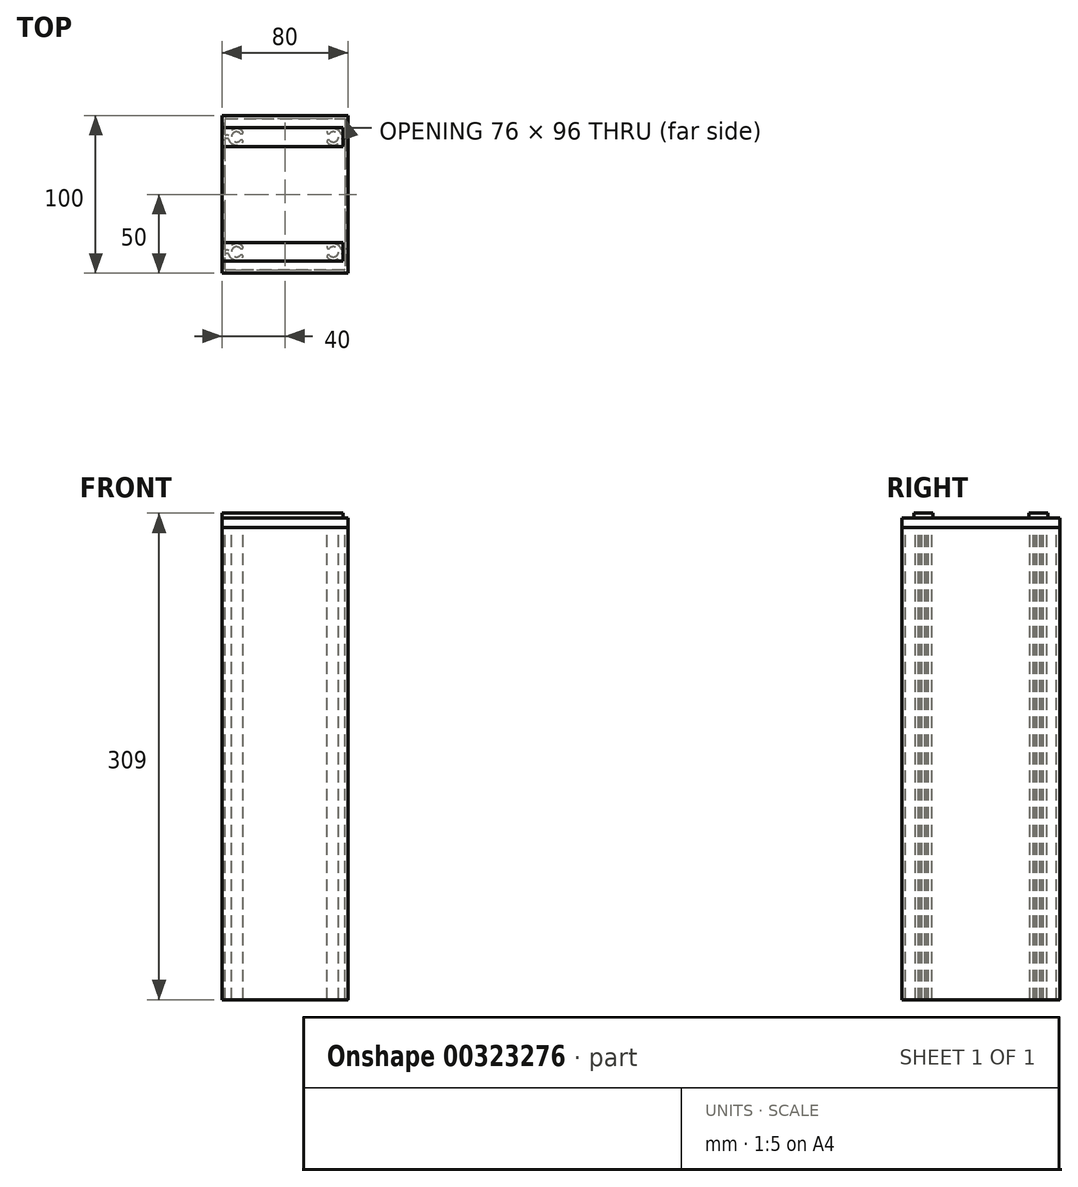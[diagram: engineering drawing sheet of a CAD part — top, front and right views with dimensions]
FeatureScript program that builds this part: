
annotation { "Feature Type Name" : "Feature", "Feature Type Description" : "" }
export const myFeature = defineFeature(function(context is Context, id is Id, definition is map)
    precondition{}
    {
        {
            var Q0;
            Q0=qCreatedBy(makeId("Top.planeOp"),FACE);
            var sketch = newSketch(context, id + "F0", { "sketchPlane" : qUnion([Q0])});
            skLineSegment(sketch, "E0", {"start": v(40, 49.5) * mm, "end": v(40, -49.5) * mm});
            skLineSegment(sketch, "E1", {"start": v(39.5, -50) * mm, "end": v(-39.5, -50) * mm});
            skLineSegment(sketch, "E2", {"start": v(-40, -49.5) * mm, "end": v(-40, 49.5) * mm});
            skLineSegment(sketch, "E3", {"start": v(-39.5, 50) * mm, "end": v(39.5, 50) * mm});
            skLineSegment(sketch, "E4", {"start": v(38, 47.5) * mm, "end": v(38, 38) * mm});
            skLineSegment(sketch, "E5", {"start": v(-37.5, 48) * mm, "end": v(37.5, 48) * mm});
            skLineSegment(sketch, "E6", {"start": v(37.5, -48) * mm, "end": v(-37.5, -48) * mm});
            skLineSegment(sketch, "E7", {"start": v(-38, -47.5) * mm, "end": v(-38, -38) * mm});
            skArc(sketch, "E8", {"start": v(28.4, -38.74) * mm, "mid": v(34, -36.5) * mm, "end": v(28.4, -34.26) * mm});
            skArc(sketch, "E9", {"start": v(28.4, -38.74) * mm, "mid": v(27.82, -38.44) * mm, "end": v(27.17, -38.57) * mm});
            skArc(sketch, "E10", {"start": v(27.17, -34.43) * mm, "mid": v(27.82, -34.56) * mm, "end": v(28.4, -34.26) * mm});
            skArc(sketch, "E11", {"start": v(26.95, -40.12) * mm, "mid": v(32.04, -41.59) * mm, "end": v(35.82, -37.87) * mm});
            skArc(sketch, "E12", {"start": v(27.17, -38.57) * mm, "mid": v(26.68, -39.29) * mm, "end": v(26.95, -40.12) * mm});
            skArc(sketch, "E13", {"start": v(26.95, -32.88) * mm, "mid": v(26.68, -33.71) * mm, "end": v(27.17, -34.43) * mm});
            skLineSegment(sketch, "E14", {"start": v(27.17, -34.43) * mm, "end": v(30.75, -36.5) * mm, "construction": true});
            skLineSegment(sketch, "E15", {"start": v(30.75, -36.5) * mm, "end": v(27.17, -38.57) * mm, "construction": true});
            skArc(sketch, "E16", {"start": v(28.4, 34.26) * mm, "mid": v(34, 36.5) * mm, "end": v(28.4, 38.74) * mm});
            skArc(sketch, "E17", {"start": v(28.4, 34.26) * mm, "mid": v(27.82, 34.56) * mm, "end": v(27.17, 34.43) * mm});
            skArc(sketch, "E18", {"start": v(27.17, 38.57) * mm, "mid": v(27.82, 38.44) * mm, "end": v(28.4, 38.74) * mm});
            skArc(sketch, "E19", {"start": v(26.95, 32.88) * mm, "mid": v(32.04, 31.41) * mm, "end": v(35.82, 35.13) * mm});
            skArc(sketch, "E20", {"start": v(27.17, 34.43) * mm, "mid": v(26.68, 33.71) * mm, "end": v(26.95, 32.88) * mm});
            skArc(sketch, "E21", {"start": v(26.95, 40.12) * mm, "mid": v(26.68, 39.29) * mm, "end": v(27.17, 38.57) * mm});
            skLineSegment(sketch, "E22", {"start": v(27.17, 38.57) * mm, "end": v(30.75, 36.5) * mm, "construction": true});
            skLineSegment(sketch, "E23", {"start": v(30.75, 36.5) * mm, "end": v(27.17, 34.43) * mm, "construction": true});
            skArc(sketch, "E24", {"start": v(-28.4, 38.74) * mm, "mid": v(-34, 36.5) * mm, "end": v(-28.4, 34.26) * mm});
            skArc(sketch, "E25", {"start": v(-27.17, 34.43) * mm, "mid": v(-27.82, 34.56) * mm, "end": v(-28.4, 34.26) * mm});
            skArc(sketch, "E26", {"start": v(-28.4, 38.74) * mm, "mid": v(-27.82, 38.44) * mm, "end": v(-27.17, 38.57) * mm});
            skArc(sketch, "E27", {"start": v(-26.95, 40.12) * mm, "mid": v(-32.04, 41.59) * mm, "end": v(-35.82, 37.87) * mm});
            skArc(sketch, "E28", {"start": v(-26.95, 32.88) * mm, "mid": v(-26.68, 33.71) * mm, "end": v(-27.17, 34.43) * mm});
            skArc(sketch, "E29", {"start": v(-27.17, 38.57) * mm, "mid": v(-26.68, 39.29) * mm, "end": v(-26.95, 40.12) * mm});
            skLineSegment(sketch, "E30", {"start": v(-27.17, 38.57) * mm, "end": v(-30.75, 36.5) * mm, "construction": true});
            skLineSegment(sketch, "E31", {"start": v(-30.75, 36.5) * mm, "end": v(-27.17, 34.43) * mm, "construction": true});
            skArc(sketch, "E32", {"start": v(-28.4, -34.26) * mm, "mid": v(-34, -36.5) * mm, "end": v(-28.4, -38.74) * mm});
            skArc(sketch, "E33", {"start": v(-27.17, -38.57) * mm, "mid": v(-27.82, -38.44) * mm, "end": v(-28.4, -38.74) * mm});
            skArc(sketch, "E34", {"start": v(-28.4, -34.26) * mm, "mid": v(-27.82, -34.56) * mm, "end": v(-27.17, -34.43) * mm});
            skArc(sketch, "E35", {"start": v(-26.95, -32.88) * mm, "mid": v(-32.04, -31.41) * mm, "end": v(-35.82, -35.13) * mm});
            skArc(sketch, "E36", {"start": v(-26.95, -40.12) * mm, "mid": v(-26.68, -39.29) * mm, "end": v(-27.17, -38.57) * mm});
            skArc(sketch, "E37", {"start": v(-27.17, -34.43) * mm, "mid": v(-26.68, -33.71) * mm, "end": v(-26.95, -32.88) * mm});
            skLineSegment(sketch, "E38", {"start": v(-27.17, -34.43) * mm, "end": v(-30.75, -36.5) * mm, "construction": true});
            skLineSegment(sketch, "E39", {"start": v(-30.75, -36.5) * mm, "end": v(-27.17, -38.57) * mm, "construction": true});
            skLineSegment(sketch, "E40", {"start": v(37.5, 35.5) * mm, "end": v(36.3, 35.5) * mm});
            skLineSegment(sketch, "E41", {"start": v(37.5, 37.5) * mm, "end": v(36.3, 37.5) * mm});
            skLineSegment(sketch, "E42", {"start": v(37.5, -35.5) * mm, "end": v(36.3, -35.5) * mm});
            skLineSegment(sketch, "E43", {"start": v(37.5, -37.5) * mm, "end": v(36.3, -37.5) * mm});
            skLineSegment(sketch, "E44", {"start": v(38, 35) * mm, "end": v(38, -35) * mm});
            skLineSegment(sketch, "E45", {"start": v(-38, 38) * mm, "end": v(-38, 47.5) * mm});
            skLineSegment(sketch, "E46", {"start": v(-36.3, 37.5) * mm, "end": v(-37.5, 37.5) * mm});
            skLineSegment(sketch, "E47", {"start": v(-36.3, 35.5) * mm, "end": v(-37.5, 35.5) * mm});
            skArc(sketch, "E48", {"start": v(35.82, 37.87) * mm, "mid": v(32.04, 41.59) * mm, "end": v(26.95, 40.12) * mm});
            skArc(sketch, "E49", {"start": v(-35.82, 35.13) * mm, "mid": v(-32.04, 31.41) * mm, "end": v(-26.95, 32.88) * mm});
            skLineSegment(sketch, "E50", {"start": v(38, -38) * mm, "end": v(38, -47.5) * mm});
            skArc(sketch, "E51", {"start": v(35.82, -35.13) * mm, "mid": v(32.04, -31.41) * mm, "end": v(26.95, -32.88) * mm});
            skLineSegment(sketch, "E52", {"start": v(-38, -35) * mm, "end": v(-38, 35) * mm});
            skArc(sketch, "E53", {"start": v(-35.82, -37.87) * mm, "mid": v(-32.04, -41.59) * mm, "end": v(-26.95, -40.12) * mm});
            skLineSegment(sketch, "E54", {"start": v(-36.3, -35.5) * mm, "end": v(-37.5, -35.5) * mm});
            skLineSegment(sketch, "E55", {"start": v(-36.3, -37.5) * mm, "end": v(-37.5, -37.5) * mm});
            skArc(sketch, "E56", {"start": v(40, 49.5) * mm, "mid": v(39.85, 49.85) * mm, "end": v(39.5, 50) * mm});
            skArc(sketch, "E57", {"start": v(39.5, -50) * mm, "mid": v(39.85, -49.85) * mm, "end": v(40, -49.5) * mm});
            skArc(sketch, "E58", {"start": v(-39.5, 50) * mm, "mid": v(-39.85, 49.85) * mm, "end": v(-40, 49.5) * mm});
            skArc(sketch, "E59", {"start": v(-40, -49.5) * mm, "mid": v(-39.85, -49.85) * mm, "end": v(-39.5, -50) * mm});
            skLineSegment(sketch, "E60", {"start": v(0, 53) * mm, "end": v(0, -53) * mm, "construction": true});
            skLineSegment(sketch, "E61", {"start": v(34.3, 36.5) * mm, "end": v(-34.3, 36.5) * mm, "construction": true});
            skLineSegment(sketch, "E62", {"start": v(34.3, -36.5) * mm, "end": v(-34.3, -36.5) * mm, "construction": true});
            skLineSegment(sketch, "E63", {"start": v(30.75, 40.05) * mm, "end": v(30.75, 32.95) * mm, "construction": true});
            skLineSegment(sketch, "E64", {"start": v(-30.75, 40.05) * mm, "end": v(-30.75, 32.95) * mm, "construction": true});
            skLineSegment(sketch, "E65", {"start": v(-30.75, -32.95) * mm, "end": v(-30.75, -40.05) * mm, "construction": true});
            skLineSegment(sketch, "E66", {"start": v(30.75, -32.95) * mm, "end": v(30.75, -40.05) * mm, "construction": true});
            skLineSegment(sketch, "E67", {"start": v(43, 0) * mm, "end": v(-43, 0) * mm, "construction": true});
            skArc(sketch, "E68", {"start": v(38, 47.5) * mm, "mid": v(37.85, 47.85) * mm, "end": v(37.5, 48) * mm});
            skArc(sketch, "E69", {"start": v(37.5, 37.5) * mm, "mid": v(37.85, 37.65) * mm, "end": v(38, 38) * mm});
            skArc(sketch, "E70", {"start": v(35.82, 37.87) * mm, "mid": v(36, 37.6) * mm, "end": v(36.3, 37.5) * mm});
            skArc(sketch, "E71", {"start": v(36.3, 35.5) * mm, "mid": v(36, 35.4) * mm, "end": v(35.82, 35.13) * mm});
            skArc(sketch, "E72", {"start": v(38, 35) * mm, "mid": v(37.85, 35.35) * mm, "end": v(37.5, 35.5) * mm});
            skArc(sketch, "E73", {"start": v(37.5, -35.5) * mm, "mid": v(37.85, -35.35) * mm, "end": v(38, -35) * mm});
            skArc(sketch, "E74", {"start": v(35.82, -35.13) * mm, "mid": v(36, -35.4) * mm, "end": v(36.3, -35.5) * mm});
            skArc(sketch, "E75", {"start": v(38, -38) * mm, "mid": v(37.85, -37.65) * mm, "end": v(37.5, -37.5) * mm});
            skArc(sketch, "E76", {"start": v(36.3, -37.5) * mm, "mid": v(36, -37.6) * mm, "end": v(35.82, -37.87) * mm});
            skArc(sketch, "E77", {"start": v(37.5, -48) * mm, "mid": v(37.85, -47.85) * mm, "end": v(38, -47.5) * mm});
            skArc(sketch, "E78", {"start": v(-36.3, 37.5) * mm, "mid": v(-36, 37.6) * mm, "end": v(-35.82, 37.87) * mm});
            skArc(sketch, "E79", {"start": v(-38, 38) * mm, "mid": v(-37.85, 37.65) * mm, "end": v(-37.5, 37.5) * mm});
            skArc(sketch, "E80", {"start": v(-37.5, 48) * mm, "mid": v(-37.85, 47.85) * mm, "end": v(-38, 47.5) * mm});
            skArc(sketch, "E81", {"start": v(-35.82, 35.13) * mm, "mid": v(-36, 35.4) * mm, "end": v(-36.3, 35.5) * mm});
            skArc(sketch, "E82", {"start": v(-37.5, 35.5) * mm, "mid": v(-37.85, 35.35) * mm, "end": v(-38, 35) * mm});
            skArc(sketch, "E83", {"start": v(-36.3, -35.5) * mm, "mid": v(-36, -35.4) * mm, "end": v(-35.82, -35.13) * mm});
            skArc(sketch, "E84", {"start": v(-38, -35) * mm, "mid": v(-37.85, -35.35) * mm, "end": v(-37.5, -35.5) * mm});
            skArc(sketch, "E85", {"start": v(-35.82, -37.87) * mm, "mid": v(-36, -37.6) * mm, "end": v(-36.3, -37.5) * mm});
            skArc(sketch, "E86", {"start": v(-37.5, -37.5) * mm, "mid": v(-37.85, -37.65) * mm, "end": v(-38, -38) * mm});
            skArc(sketch, "E87", {"start": v(-38, -47.5) * mm, "mid": v(-37.85, -47.85) * mm, "end": v(-37.5, -48) * mm});
            skSolve(sketch);
        }
        {
            var Q0;
            Q0=makeQuery(id+"F0.imprint","IMPRINT",FACE,{"disambiguationData":[TD([[makeQuery(id+"F0.imprint","IMPRINT",EDGE,{"derivedFrom":sQuery(id+"F0.wireOp",EDGE,"E0")}),-1.0]])]});
            extrude(context, id + "F1", {"entities" : qUnion([Q0]), "oppositeDirection" : true, "depth" : 300 * mm});
        }
        {
            var Q0;
            Q0=makeQuery(id+"F1.opExtrude","CAP_FACE",FACE,{"disambiguationData":[OSD([sQuery(id+"F0.wireOp",EDGE,"E0"),sQuery(id+"F0.wireOp",EDGE,"E1"),sQuery(id+"F0.wireOp",EDGE,"E2"),sQuery(id+"F0.wireOp",EDGE,"E3"),sQuery(id+"F0.wireOp",EDGE,"E4"),sQuery(id+"F0.wireOp",EDGE,"E5"),sQuery(id+"F0.wireOp",EDGE,"E6"),sQuery(id+"F0.wireOp",EDGE,"E7"),sQuery(id+"F0.wireOp",EDGE,"E8"),sQuery(id+"F0.wireOp",EDGE,"E9"),sQuery(id+"F0.wireOp",EDGE,"E10"),sQuery(id+"F0.wireOp",EDGE,"E11"),sQuery(id+"F0.wireOp",EDGE,"E12"),sQuery(id+"F0.wireOp",EDGE,"E13"),sQuery(id+"F0.wireOp",EDGE,"E16"),sQuery(id+"F0.wireOp",EDGE,"E17"),sQuery(id+"F0.wireOp",EDGE,"E18"),sQuery(id+"F0.wireOp",EDGE,"E19"),sQuery(id+"F0.wireOp",EDGE,"E20"),sQuery(id+"F0.wireOp",EDGE,"E21"),sQuery(id+"F0.wireOp",EDGE,"E24"),sQuery(id+"F0.wireOp",EDGE,"E25"),sQuery(id+"F0.wireOp",EDGE,"E26"),sQuery(id+"F0.wireOp",EDGE,"E27"),sQuery(id+"F0.wireOp",EDGE,"E28"),sQuery(id+"F0.wireOp",EDGE,"E29"),sQuery(id+"F0.wireOp",EDGE,"E32"),sQuery(id+"F0.wireOp",EDGE,"E33"),sQuery(id+"F0.wireOp",EDGE,"E34"),sQuery(id+"F0.wireOp",EDGE,"E35"),sQuery(id+"F0.wireOp",EDGE,"E36"),sQuery(id+"F0.wireOp",EDGE,"E37"),sQuery(id+"F0.wireOp",EDGE,"E40"),sQuery(id+"F0.wireOp",EDGE,"E41"),sQuery(id+"F0.wireOp",EDGE,"E42"),sQuery(id+"F0.wireOp",EDGE,"E43"),sQuery(id+"F0.wireOp",EDGE,"E44"),sQuery(id+"F0.wireOp",EDGE,"E45"),sQuery(id+"F0.wireOp",EDGE,"E46"),sQuery(id+"F0.wireOp",EDGE,"E47"),sQuery(id+"F0.wireOp",EDGE,"E48"),sQuery(id+"F0.wireOp",EDGE,"E49"),sQuery(id+"F0.wireOp",EDGE,"E50"),sQuery(id+"F0.wireOp",EDGE,"E51"),sQuery(id+"F0.wireOp",EDGE,"E52"),sQuery(id+"F0.wireOp",EDGE,"E53"),sQuery(id+"F0.wireOp",EDGE,"E54"),sQuery(id+"F0.wireOp",EDGE,"E55"),sQuery(id+"F0.wireOp",EDGE,"E56"),sQuery(id+"F0.wireOp",EDGE,"E57"),sQuery(id+"F0.wireOp",EDGE,"E58"),sQuery(id+"F0.wireOp",EDGE,"E59"),sQuery(id+"F0.wireOp",EDGE,"E68"),sQuery(id+"F0.wireOp",EDGE,"E69"),sQuery(id+"F0.wireOp",EDGE,"E70"),sQuery(id+"F0.wireOp",EDGE,"E71"),sQuery(id+"F0.wireOp",EDGE,"E72"),sQuery(id+"F0.wireOp",EDGE,"E73"),sQuery(id+"F0.wireOp",EDGE,"E74"),sQuery(id+"F0.wireOp",EDGE,"E75"),sQuery(id+"F0.wireOp",EDGE,"E76"),sQuery(id+"F0.wireOp",EDGE,"E77"),sQuery(id+"F0.wireOp",EDGE,"E78"),sQuery(id+"F0.wireOp",EDGE,"E79"),sQuery(id+"F0.wireOp",EDGE,"E80"),sQuery(id+"F0.wireOp",EDGE,"E81"),sQuery(id+"F0.wireOp",EDGE,"E82"),sQuery(id+"F0.wireOp",EDGE,"E83"),sQuery(id+"F0.wireOp",EDGE,"E84"),sQuery(id+"F0.wireOp",EDGE,"E85"),sQuery(id+"F0.wireOp",EDGE,"E86"),sQuery(id+"F0.wireOp",EDGE,"E87")])],"isStart":true});
            var sketch = newSketch(context, id + "F2", { "sketchPlane" : qUnion([Q0])});
            skLineSegment(sketch, "E88.bottom", {"start": v(40, 50) * mm, "end": v(-40, 50) * mm});
            skLineSegment(sketch, "E88.top", {"start": v(40, -50) * mm, "end": v(-40, -50) * mm});
            skLineSegment(sketch, "E88.left", {"start": v(40, 50) * mm, "end": v(40, -50) * mm});
            skLineSegment(sketch, "E88.right", {"start": v(-40, 50) * mm, "end": v(-40, -50) * mm});
            skSolve(sketch);
        }
        {
            var Q0;
            Q0 = qSketchRegion(id + "F2", true);
            extrude(context, id + "F3", {"entities" : qUnion([Q0]), "depth" : 9 * mm});
        }
        {
            var Q0;
            Q0=makeQuery(id+"F3.opExtrude","SWEPT_FACE",FACE,{"disambiguationData":[OSD([sQuery(id+"F2.wireOp",EDGE,"E88.left")])]});
            var sketch = newSketch(context, id + "F4", { "sketchPlane" : qUnion([Q0])});
            skLineSegment(sketch, "E89.bottom", {"start": v(-50, 9) * mm, "end": v(-42.5, 9) * mm});
            skLineSegment(sketch, "E89.top", {"start": v(-50, 6) * mm, "end": v(-42.5, 6) * mm});
            skLineSegment(sketch, "E89.left", {"start": v(-50, 9) * mm, "end": v(-50, 6) * mm});
            skLineSegment(sketch, "E89.right", {"start": v(-42.5, 9) * mm, "end": v(-42.5, 6) * mm});
            skLineSegment(sketch, "E90.bottom", {"start": v(-30.5, 9) * mm, "end": v(30.5, 9) * mm});
            skLineSegment(sketch, "E90.top", {"start": v(-30.5, 6) * mm, "end": v(30.5, 6) * mm});
            skLineSegment(sketch, "E90.left", {"start": v(-30.5, 9) * mm, "end": v(-30.5, 6) * mm});
            skLineSegment(sketch, "E90.right", {"start": v(30.5, 9) * mm, "end": v(30.5, 6) * mm});
            skLineSegment(sketch, "E91.bottom", {"start": v(42.5, 9) * mm, "end": v(50, 9) * mm});
            skLineSegment(sketch, "E91.top", {"start": v(42.5, 6) * mm, "end": v(50, 6) * mm});
            skLineSegment(sketch, "E91.left", {"start": v(42.5, 9) * mm, "end": v(42.5, 6) * mm});
            skLineSegment(sketch, "E91.right", {"start": v(50, 9) * mm, "end": v(50, 6) * mm});
            skLineSegment(sketch, "E92", {"start": v(-42.5, 6) * mm, "end": v(-30.5, 6) * mm, "construction": true});
            skLineSegment(sketch, "E93", {"start": v(30.5, 6) * mm, "end": v(42.5, 6) * mm, "construction": true});
            skLineSegment(sketch, "E94", {"start": v(0, 0) * mm, "end": v(0, 6) * mm, "construction": true});
            skLineSegment(sketch, "E95", {"start": v(-36.5, 6) * mm, "end": v(-36.5, 0) * mm, "construction": true});
            skLineSegment(sketch, "E96", {"start": v(36.5, 6) * mm, "end": v(36.5, 0) * mm, "construction": true});
            skSolve(sketch);
        }
        {
            var Q0;
            Q0=makeQuery(id+"F4.imprint","IMPRINT",FACE,{"disambiguationData":[TD([[makeQuery(id+"F4.imprint","IMPRINT",EDGE,{"derivedFrom":sQuery(id+"F4.wireOp",EDGE,"E89.bottom")}),1.0]])]});
            var Q1;
            Q1=makeQuery(id+"F4.imprint","IMPRINT",FACE,{"disambiguationData":[TD([[makeQuery(id+"F4.imprint","IMPRINT",EDGE,{"derivedFrom":sQuery(id+"F4.wireOp",EDGE,"E90.bottom")}),1.0]])]});
            var Q2;
            Q2=makeQuery(id+"F4.imprint","IMPRINT",FACE,{"disambiguationData":[TD([[makeQuery(id+"F4.imprint","IMPRINT",EDGE,{"derivedFrom":sQuery(id+"F4.wireOp",EDGE,"E91.bottom")}),1.0]])]});
            extrude(context, id + "F5", {"entities" : qUnion([Q0, Q1, Q2]), "operationType" : NewBodyOperationType.REMOVE, "endBound" : BoundingType.THROUGH_ALL, "oppositeDirection" : true, "depth" : 25 * mm});
        }
        {
            var Q0;
            Q0=makeQuery(id+"F5.boolean.opBoolean","COPY",FACE,{"derivedFrom":makeQuery(id+"F5.opExtrude","SWEPT_FACE",FACE,{"disambiguationData":[OSD([sQuery(id+"F4.wireOp",EDGE,"E90.top")])]})});
            var sketch = newSketch(context, id + "F6", { "sketchPlane" : qUnion([Q0])});
            skLineSegment(sketch, "E97.bottom", {"start": v(37, 50) * mm, "end": v(40, 50) * mm});
            skLineSegment(sketch, "E97.top", {"start": v(37, -50) * mm, "end": v(40, -50) * mm});
            skLineSegment(sketch, "E97.left", {"start": v(37, 50) * mm, "end": v(37, -50) * mm});
            skLineSegment(sketch, "E97.right", {"start": v(40, 50) * mm, "end": v(40, -50) * mm});
            skSolve(sketch);
        }
        {
            var Q0;
            Q0 = qSketchRegion(id + "F6", true);
            var Q1;
            Q1=makeQuery(id+"F5.boolean.opBoolean","COPY",FACE,{"derivedFrom":makeQuery(id+"F5.opExtrude","SWEPT_FACE",FACE,{"disambiguationData":[OSD([sQuery(id+"F4.wireOp",EDGE,"E89.top")])]})});
            extrude(context, id + "F7", {"entities" : qUnion([Q0]), "operationType" : NewBodyOperationType.REMOVE, "endBoundEntityFace" : qUnion([Q1]), "depth" : 25 * mm});
        }
    });
